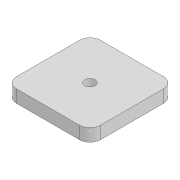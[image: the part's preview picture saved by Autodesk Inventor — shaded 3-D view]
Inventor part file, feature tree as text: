
AUTODESK INVENTOR PART (.ipt)
format: ipt  version: 2020 (Build 240168000, 168)  size: 90,112 bytes
history: native  units: mm
features: sketch x2, other x1, extrude x1, fillet x1
ambient origin geometry x8: Origin, YZ Plane, XZ Plane, XY Plane, X Axis, Y Axis, Z Axis, Center Point
bodies: Body1 (feature_tree)
feature tree (5):
  other  "Sólido1"
  extrude  "Extrusão1"  Depth=80.0mm
  fillet  "Arredondamento1"  Radius=10.0mm
  sketch  "Esboço2"  dims[d3=12.0mm d4=0.0mm d5=10.0mm]
  sketch  "Esboço1"  dims[d0=80.0mm d1=80.0mm d2=10.0mm]
